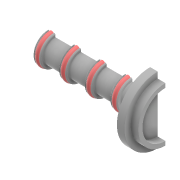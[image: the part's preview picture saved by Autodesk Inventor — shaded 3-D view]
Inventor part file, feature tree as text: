
AUTODESK INVENTOR PART (.ipt)
format: ipt  version: 2021 (Build 250183000, 183)  size: 518,144 bytes
history: native  units: in
note: dims shown in document units (in); Inventor stores cm internally (conversion verified against a paired STEP export)
features: projected_geometry x8, revolve x3, chamfer x2, split x2, sketch x2, fillet x1
ambient origin geometry x8: Origin, YZ Plane, XZ Plane, XY Plane, X Axis, Y Axis, Z Axis, Center Point
bodies: Solid1 (feature_tree), Solid4 (feature_tree)
feature tree (18):
  revolve  "Revolution1"  [1 undecoded]
  revolve  "Revolution2"  [1 undecoded]
  revolve  "Revolution5"  [1 undecoded]
  chamfer  "Chamfer1"  Distance=0.1378in
  chamfer  "Chamfer2"  Distance=0.2559in
  fillet  "Fillet6"  [1 undecoded]
  split  "Split1"
  split  "Split2"
  sketch  "Sketch1"  dims[d2=0.0591in d3=0.0591in]
  sketch  "Sketch2"  dims[d4=0.0591in d5=0.0591in d9=0.1378in d10=0.1378in d14=0.2559in d15=90.0deg d31=90.0deg d52=90.0deg d53=0.0059in d54=0.0787in d55=45.0deg d57=0.0059in d58=0.0787in d59=45.0deg d60=0.2087in d61=0.1772in d62=0.0591in d63=0.0984in d64=0.0394in d65=0.1575in d73=0.0118in d74=0.0118in d75=0.0217in d76=0.0118in d77=0.0118in d78=0.0217in d79=0.0118in d80=0.0118in d81=0.0217in d82=0.037in d83=0.0079in d84=0.0079in d85=0.0059in d86=1.1811in d88=0.1969in d89=0.3937in d91=0.3937in d94=0.002in d95=0.0591in d96=0.1378in d102=0.1969in d107=0.7874in d109=0.1969in d110=0.3937in d112=0.3937in d114=0.0906in d115=0.1146in]
  projected_geometry  "Projected Loop1"
  projected_geometry  "Projected Loop2"
  projected_geometry  "Projected Loop3"
  projected_geometry  "Projected Loop4"
  projected_geometry  "Projected Loop5"
  projected_geometry  "Project Cut Edges1"
  projected_geometry  "Project Cut Edges2"
  projected_geometry  "Project Cut Edges3"
note: 4 required parameter values undecoded (feature->parameter linkage not recoverable at this tier; creation-order binding heuristic only, values carry confidence <= 0.55)